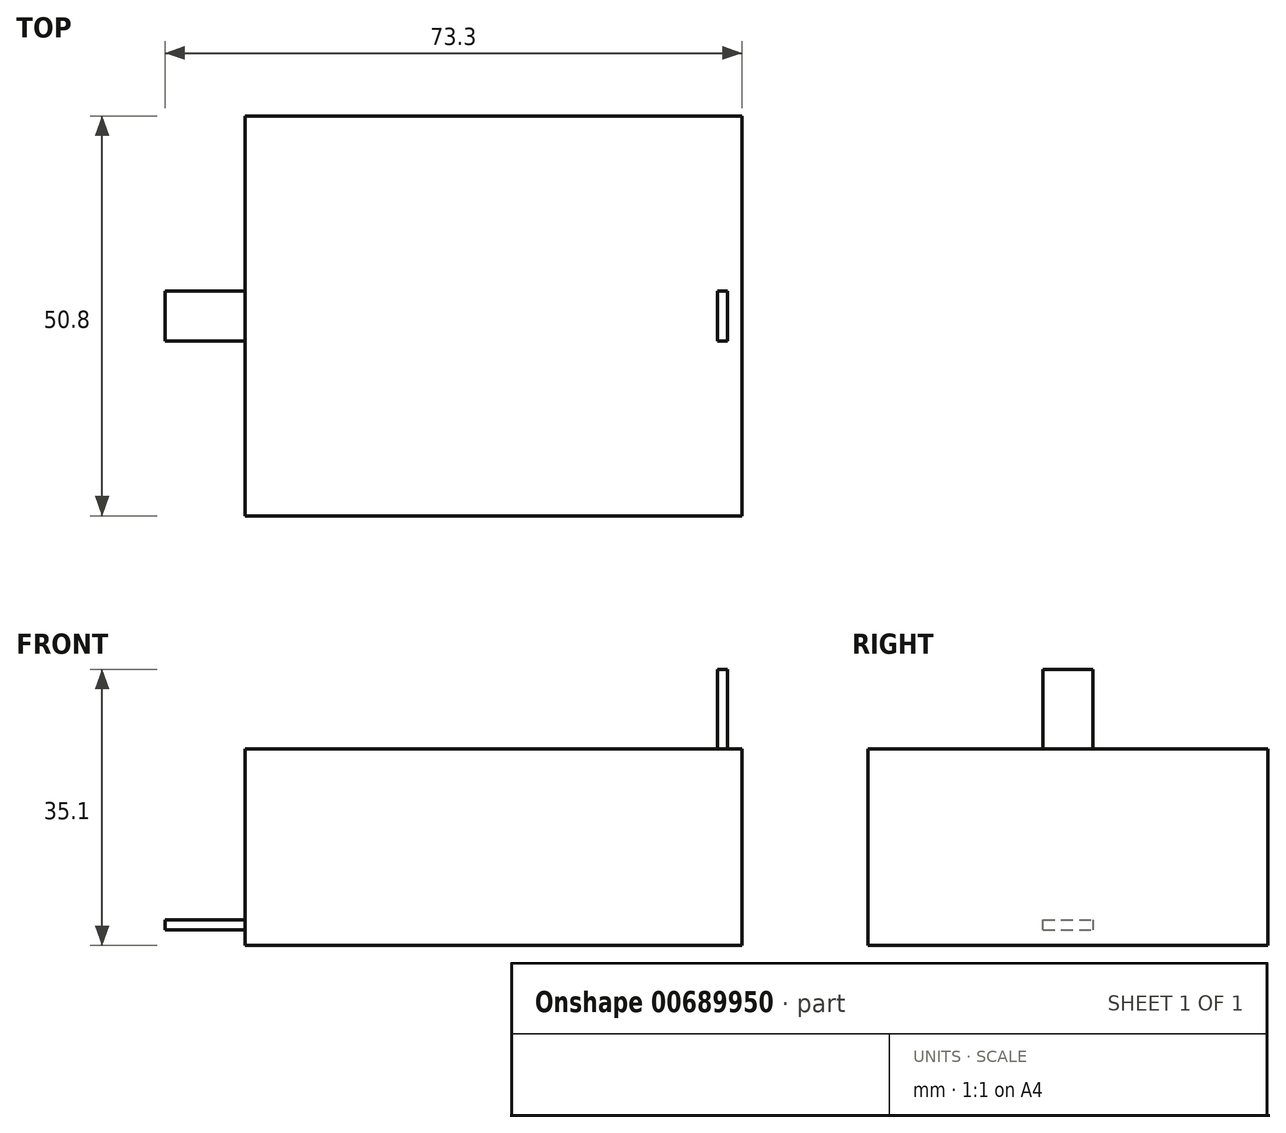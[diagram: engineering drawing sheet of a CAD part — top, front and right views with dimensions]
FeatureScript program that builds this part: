
annotation { "Feature Type Name" : "Feature", "Feature Type Description" : "" }
export const myFeature = defineFeature(function(context is Context, id is Id, definition is map)
    precondition{}
    {
        {
            var Q0;
            Q0=qCreatedBy(makeId("Front.planeOp"),FACE);
            var sketch = newSketch(context, id + "F0", { "sketchPlane" : qUnion([Q0])});
            skLineSegment(sketch, "E0.bottom", {"start": v(-31.57, 12.48) * mm, "end": v(31.57, 12.48) * mm});
            skLineSegment(sketch, "E0.top", {"start": v(-31.57, -12.48) * mm, "end": v(31.57, -12.48) * mm});
            skLineSegment(sketch, "E0.left", {"start": v(-31.57, 12.48) * mm, "end": v(-31.57, -12.48) * mm});
            skLineSegment(sketch, "E0.right", {"start": v(31.57, 12.48) * mm, "end": v(31.57, -12.48) * mm});
            skPoint(sketch, "E0.middle", {"position": v(0, 0) * mm});
            skSolve(sketch);
        }
        {
            var Q0;
            Q0=makeQuery(id+"F0.imprint","IMPRINT",FACE,{"disambiguationData":[TD([[makeQuery(id+"F0.imprint","IMPRINT",EDGE,{"derivedFrom":sQuery(id+"F0.wireOp",EDGE,"E0.bottom")}),-1.0]])]});
            var Q1;
            Q1=makeQuery(id+"F2.imprint","IMPRINT",FACE,{"disambiguationData":[TD([[makeQuery(id+"F2.imprint","IMPRINT",EDGE,{"derivedFrom":sQuery(id+"F2.wireOp",EDGE,"E1.bottom")}),-1.0]])]});
            var Q2;
            Q2=makeQuery(id+"F4.imprint","IMPRINT",FACE,{"disambiguationData":[TD([[makeQuery(id+"F4.imprint","IMPRINT",EDGE,{"derivedFrom":sQuery(id+"F4.wireOp",EDGE,"E2.bottom")}),-1.0]])]});
            extrude(context, id + "F1", {"entities" : qUnion([Q0, Q1, Q2]), "endBound" : BoundingType.SYMMETRIC, "depth" : 50.8 * mm, "offsetDistance" : 25.4 * mm});
        }
        {
            var Q0;
            Q0=qCreatedBy(makeId("Front.planeOp"),FACE);
            var sketch = newSketch(context, id + "F2", { "sketchPlane" : qUnion([Q0])});
            skLineSegment(sketch, "E1.bottom", {"start": v(28.45, 12.46) * mm, "end": v(28.45, 22.62) * mm});
            skLineSegment(sketch, "E1.top", {"start": v(29.72, 12.46) * mm, "end": v(29.72, 22.62) * mm});
            skLineSegment(sketch, "E1.left", {"start": v(28.45, 12.46) * mm, "end": v(29.72, 12.46) * mm});
            skLineSegment(sketch, "E1.right", {"start": v(28.45, 22.62) * mm, "end": v(29.72, 22.62) * mm});
            skSolve(sketch);
        }
        {
            var Q0;
            Q0=qSketchRegion(id+"F2",true);
            extrude(context, id + "F3", {"entities" : qUnion([Q0]), "operationType" : NewBodyOperationType.ADD, "endBound" : BoundingType.SYMMETRIC, "depth" : 6.35 * mm, "offsetDistance" : 25.4 * mm});
        }
        {
            var Q0;
            Q0=qCreatedBy(makeId("Front.planeOp"),FACE);
            var sketch = newSketch(context, id + "F4", { "sketchPlane" : qUnion([Q0])});
            skLineSegment(sketch, "E2.bottom", {"start": v(-31.57, -10.47) * mm, "end": v(-41.73, -10.47) * mm});
            skLineSegment(sketch, "E2.top", {"start": v(-31.57, -9.2) * mm, "end": v(-41.73, -9.2) * mm});
            skLineSegment(sketch, "E2.left", {"start": v(-31.57, -10.47) * mm, "end": v(-31.57, -9.2) * mm});
            skLineSegment(sketch, "E2.right", {"start": v(-41.73, -10.47) * mm, "end": v(-41.73, -9.2) * mm});
            skSolve(sketch);
        }
        {
            var Q0;
            Q0=qSketchRegion(id+"F4",true);
            extrude(context, id + "F5", {"entities" : qUnion([Q0]), "operationType" : NewBodyOperationType.ADD, "endBound" : BoundingType.SYMMETRIC, "depth" : 6.35 * mm, "offsetDistance" : 25.4 * mm});
        }
    });
